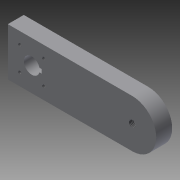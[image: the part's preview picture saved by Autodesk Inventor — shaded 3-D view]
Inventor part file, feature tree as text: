
AUTODESK INVENTOR PART (.ipt)
format: ipt  version: 2015 SP1 (Build 190203100, 203)  size: 108,032 bytes
history: native  units: in
note: dims shown in document units (in); Inventor stores cm internally (conversion verified against a paired STEP export)
features: sketch x3, hole x2, extrude x1
ambient origin geometry x8: Origin, YZ Plane, XZ Plane, XY Plane, X Axis, Y Axis, Z Axis, Center Point
bodies: Body1 (feature_tree)
feature tree (6):
  extrude  "Extrusion2"  Depth=1.0in
  hole  "Hole1"  [1 undecoded]
  hole  "Hole3"  [1 undecoded]
  sketch  "Sketch1"  dims[d0=3.0in d4=1.0in]
  sketch  "Sketch2"  dims[d13=0.1in d14=0.25in]
  sketch  "Sketch4"  dims[d15=6.3in d16=0.13in d17=1.5in d18=1.0in d19=0.0in d20=1.5in d21=1.5in d22=0.75in d23=0.75in d24=0.196in d25=0.75in d26=0.375in d27=0.25in d28=0.5635in d29=1.0in d30=0.8108in d38=0.417in d39=1.0in d40=0.375in d41=0.25in d42=0.5635in d43=1.385in d44=0.8108in]
note: 2 required parameter values undecoded (feature->parameter linkage not recoverable at this tier; creation-order binding heuristic only, values carry confidence <= 0.55)
